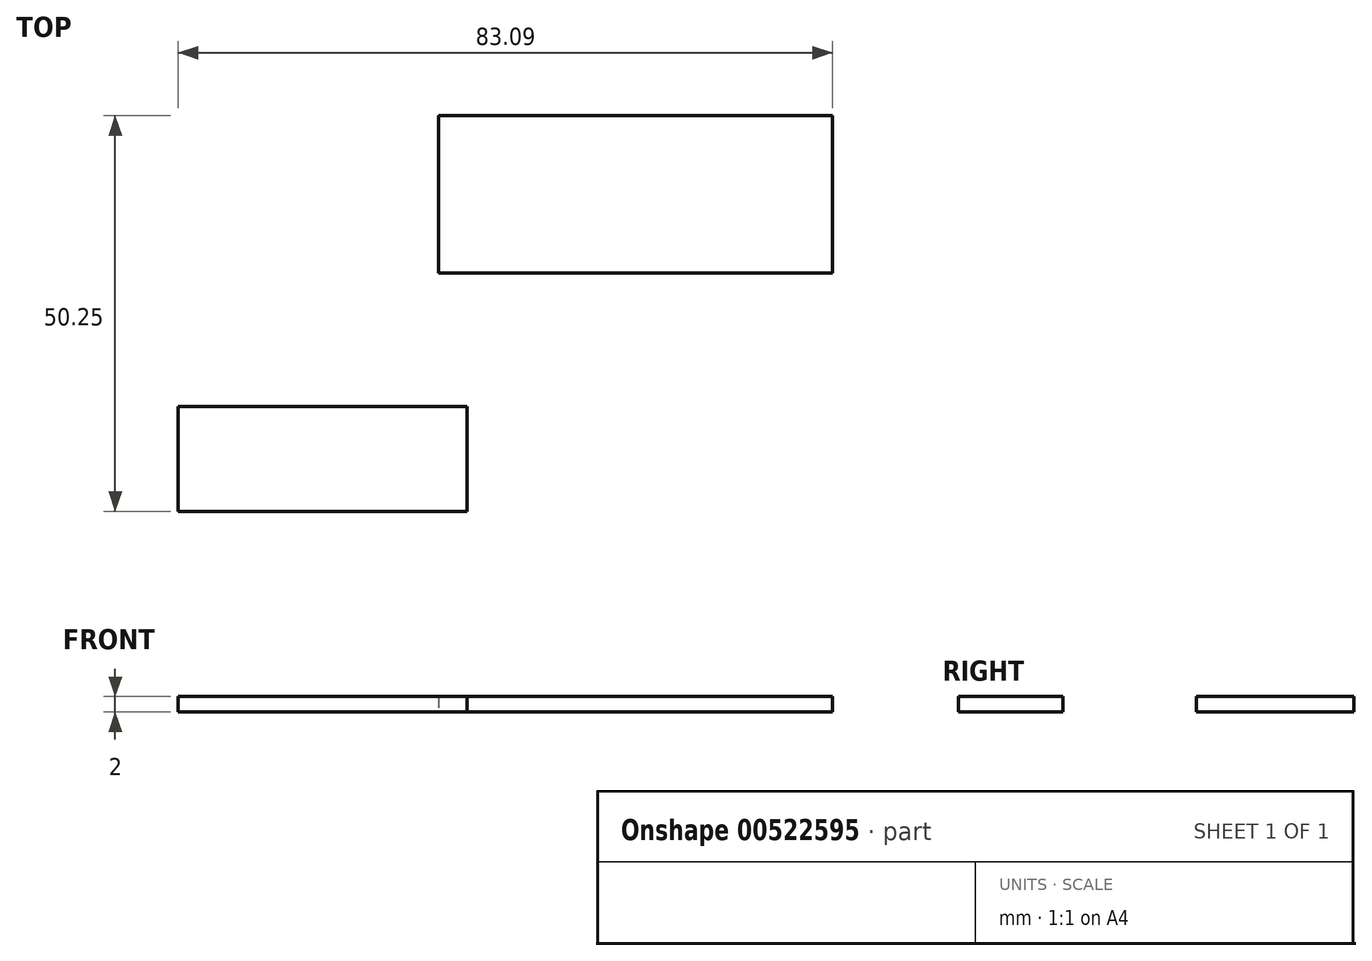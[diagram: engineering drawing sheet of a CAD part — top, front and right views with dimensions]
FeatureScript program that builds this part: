
annotation { "Feature Type Name" : "Feature", "Feature Type Description" : "" }
export const myFeature = defineFeature(function(context is Context, id is Id, definition is map)
    precondition{}
    {
        {
            var Q0;
            Q0=qCreatedBy(makeId("Top.planeOp"),FACE);
            var sketch = newSketch(context, id + "F0", { "sketchPlane" : qUnion([Q0])});
            skLineSegment(sketch, "E0.bottom", {"start": v(-25, 10) * mm, "end": v(25, 10) * mm});
            skLineSegment(sketch, "E0.top", {"start": v(-25, -10) * mm, "end": v(25, -10) * mm});
            skLineSegment(sketch, "E0.left", {"start": v(-25, 10) * mm, "end": v(-25, -10) * mm});
            skLineSegment(sketch, "E0.right", {"start": v(25, 10) * mm, "end": v(25, -10) * mm});
            skPoint(sketch, "E0.middle", {"position": v(0, 0) * mm});
            skSolve(sketch);
        }
        {
            var Q0;
            Q0=makeQuery(id+"F0.imprint","IMPRINT",FACE,{"disambiguationData":[TD([[makeQuery(id+"F0.imprint","IMPRINT",EDGE,{"derivedFrom":sQuery(id+"F0.wireOp",EDGE,"E0.bottom")}),-1.0]])]});
            extrude(context, id + "F1", {"entities" : qUnion([Q0]), "depth" : 2 * mm, "offsetDistance" : 25 * mm});
        }
        {
            var Q0;
            Q0=qCreatedBy(makeId("Top.planeOp"),FACE);
            var sketch = newSketch(context, id + "F2", { "sketchPlane" : qUnion([Q0])});
            skLineSegment(sketch, "E1.bottom", {"start": v(-58.09, -26.95) * mm, "end": v(-21.42, -26.95) * mm});
            skLineSegment(sketch, "E1.top", {"start": v(-58.09, -40.25) * mm, "end": v(-21.42, -40.25) * mm});
            skLineSegment(sketch, "E1.left", {"start": v(-58.09, -26.95) * mm, "end": v(-58.09, -40.25) * mm});
            skLineSegment(sketch, "E1.right", {"start": v(-21.42, -26.95) * mm, "end": v(-21.42, -40.25) * mm});
            skSolve(sketch);
        }
        {
            var Q0;
            Q0 = qSketchRegion(id + "F2", true);
            extrude(context, id + "F3", {"entities" : qUnion([Q0]), "depth" : 2 * mm, "offsetDistance" : 25 * mm});
        }
    });
